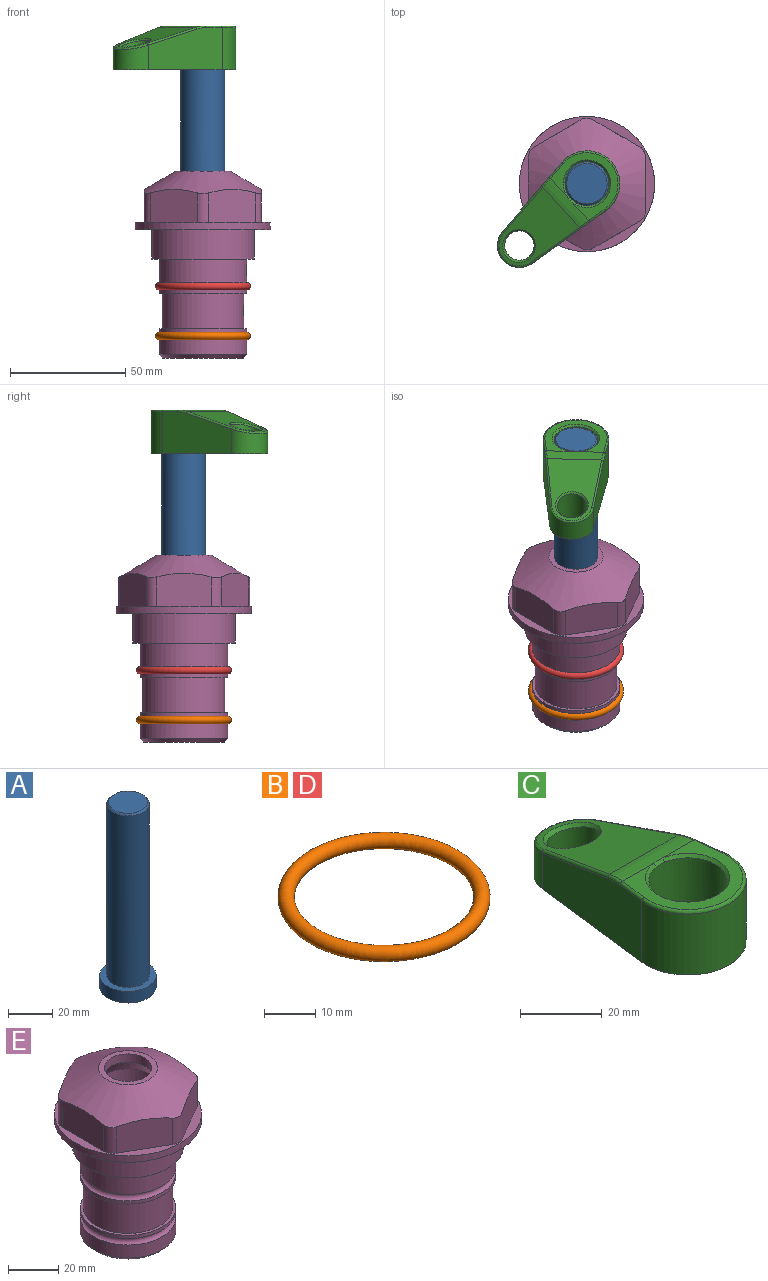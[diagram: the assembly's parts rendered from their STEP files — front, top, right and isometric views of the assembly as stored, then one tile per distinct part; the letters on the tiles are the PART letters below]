
ASSEMBLY  parts=5 mates=4
PART A: 6 faces, bbox 25.4x25.4x101.6 mm
  f0: plane 17.46x17.46mm, normal (0,0,1), area 239.5mm2, adj f5
  f1: plane 25.4x25.4mm, normal (0,0,-1), area 506.7mm2, adj f2
  f2: cylinder r=12.7mm len=25.4mm, axis (0,0,1), area 506.7mm2, adj f1,f3
  f3: plane 25.4x25.4mm, normal (0,0,1), area 221.7mm2, adj f2,f4
  f4: cylinder r=9.53mm len=94.46mm, axis (0,0,1), area 5653mm2, adj f3,f5
  f5: cone r=8.73mm half-angle=45deg, axis (0,0,-1), area 64.4mm2, adj f0,f4
PART B: 1 faces, bbox 44.7x44.7x3.2 mm
  f0: torus R=19.05mm, axis (0,0,1), area 1193.9mm2
PART C: 31 faces, bbox 31.7x65.5x19.8 mm
  f0: plane 39.12x18.26mm, normal (0.99,0.12,0), area 612.2mm2, adj f1,f4,f7,f11,f13,f15
  f1: cylinder r=9.53mm len=18.91mm, axis (0,0,-1), area 296.1mm2, adj f0,f2,f7,f17
  f2: plane 39.12x18.26mm, normal (-0.99,0.12,0), area 612.2mm2, adj f1,f4,f7,f12,f14,f16
  f3: cylinder r=6.35mm len=12.7mm, axis (0,0,-1), area 362.4mm2, adj f7,f18
  f4: cylinder r=14.29mm len=28.58mm, axis (0,0,-1), area 882.2mm2, adj f0,f2,f7,f10
  f5: cylinder r=9.53mm len=19.05mm, axis (0,0,-1), area 1092.6mm2, adj f7,f19,f20
  f6: plane 26.99x23.69mm, normal (0,0,1), area 216.2mm2, adj f9,f10,f11,f12,f19
  f7: plane 63.5x28.58mm, normal (0,0,-1), area 661.8mm2, adj f0,f1,f2,f3,f4,f5,f22,f23
  f8: plane 33.52x23.6mm, normal (0,0.26,0.97), area 486mm2, adj f9,f15,f16,f17,f18
  f9: cylinder r=19.05mm len=24.72mm, axis (1,0,0), area 120.4mm2, adj f6,f8,f13,f14,f20
  f10: torus R=13.49mm, axis (0,0,1), area 59mm2, adj f4,f6,f11,f12
  f11: cylinder r=0.79mm len=8.67mm, axis (0.12,-0.99,0), area 10.8mm2, adj f0,f6,f10,f13
  f12: cylinder r=0.79mm len=8.67mm, axis (0.12,0.99,0), area 10.8mm2, adj f2,f6,f10,f14
  f13: bspline ~4.95x1.42mm, area 6.1mm2, adj f0,f9,f11,f15
  f14: bspline ~4.95x1.42mm, area 6.1mm2, adj f2,f9,f12,f16
  f15: cylinder r=0.79mm len=25.95mm, axis (0.12,-0.96,0.26), area 32.9mm2, adj f0,f8,f13,f17
  f16: cylinder r=0.79mm len=25.95mm, axis (0.12,0.96,-0.26), area 32.9mm2, adj f2,f8,f14,f17
  f17: bspline ~18.91x8.38mm, area 30mm2, adj f1,f8,f15,f16
  f18: bspline ~14.29x14.29mm, area 48.3mm2, adj f3,f8
  f19: cone r=9.53mm half-angle=45deg, axis (0,0,1), area 66.5mm2, adj f5,f6,f20
  f20: bspline ~3.22x0.96mm, area 3.5mm2, adj f5,f9,f19
  f21: plane 2.75x2.72mm, normal (0,0,-1), area 2.9mm2, adj f23,f25,f28
  f22: plane 23.05x15.88mm, normal (-0.99,-0.12,0), area 323.6mm2, adj f7,f25,f26,f27,f28,f29
  f23: plane 23.05x15.88mm, normal (0.99,-0.12,0), area 323.6mm2, adj f7,f21,f25,f27,f28,f30
  f24: cylinder r=9.53mm len=10.69mm, axis (0,0,-1), area 114.7mm2, adj f7,f27,f29,f30
  f25: cylinder r=12.7mm len=20.59mm, axis (0,0,-1), area 381.1mm2, adj f7,f21,f22,f23,f26,f28
  f26: plane 2.75x2.72mm, normal (0,0,-1), area 2.9mm2, adj f22,f25,f28
  f27: plane 19.72x18.37mm, normal (0,-0.26,-0.97), area 291.8mm2, adj f22,f23,f24,f28,f29,f30
  f28: cylinder r=15.88mm len=19.92mm, axis (1,0,0), area 54.8mm2, adj f21,f22,f23,f25,f26,f27
  f29: cylinder r=1.59mm len=11mm, axis (0,0,-1), area 34.7mm2, adj f7,f22,f24,f27
  f30: cylinder r=1.59mm len=11mm, axis (0,0,-1), area 34.7mm2, adj f7,f23,f24,f27
PART D: same geometry as B
PART E: 36 faces, bbox 58.7x58.7x81 mm
  f0: cylinder r=17.78mm len=35.56mm, axis (0,0,1), area 1670.8mm2, adj f23,f24,f31
  f1: cylinder r=19.05mm len=38.1mm, axis (0,0,1), area 1191.9mm2, adj f26,f27,f30
  f2: plane 58.66x58.66mm, normal (0,0,-1), area 1150.6mm2, adj f3,f28
  f3: cylinder r=29.33mm len=58.66mm, axis (0,0,-1), area 585.1mm2, adj f2,f4
  f4: plane 58.66x58.66mm, normal (0,0,1), area 475.9mm2, adj f3,f5,f6,f7,f8,f9,f10,f11
  f5: plane 20.32x14.34mm, normal (-0.5,0.87,0), area 324.4mm2, adj f4,f15,f16,f17
  f6: plane 20.32x14.34mm, normal (0.5,0.87,0), area 324.4mm2, adj f4,f14,f15,f17
  f7: plane 23.48x14.34mm, normal (1,0,0), area 324.4mm2, adj f4,f13,f14,f17
  f8: plane 20.32x14.34mm, normal (0.5,-0.87,0), area 324.4mm2, adj f4,f12,f13,f17
  f9: plane 20.32x14.34mm, normal (-0.5,-0.87,0), area 324.4mm2, adj f4,f11,f12,f17
  f10: plane 23.48x14.34mm, normal (-1,0,0), area 324.4mm2, adj f4,f11,f16,f17
  f11: cylinder r=5.08mm len=12.85mm, axis (0,0,-1), area 67.2mm2, adj f4,f9,f10,f17
  f12: cylinder r=5.08mm len=12.85mm, axis (0,0,-1), area 67.2mm2, adj f4,f8,f9,f17
  f13: cylinder r=5.08mm len=12.85mm, axis (0,0,-1), area 67.2mm2, adj f4,f7,f8,f17
  f14: cylinder r=5.08mm len=12.85mm, axis (0,0,-1), area 67.2mm2, adj f4,f6,f7,f17
  f15: cylinder r=5.08mm len=12.85mm, axis (0,0,-1), area 67.2mm2, adj f4,f5,f6,f17
  f16: cylinder r=5.08mm len=12.85mm, axis (0,0,-1), area 67.2mm2, adj f4,f5,f10,f17
  f17: cone r=11.73mm half-angle=60deg, axis (0,0,-1), area 2071.8mm2, adj f5,f6,f7,f8,f9,f10,f11,f12
  f18: plane 23.46x23.46mm, normal (0,0,1), area 147.4mm2, adj f17,f35
  f19: plane 34.93x34.93mm, normal (0,0,-1), area 958mm2, adj f29
  f20: cylinder r=19.05mm len=38.1mm, axis (0,0,1), area 760.1mm2, adj f21,f29
  f21: torus R=19.05mm, axis (0,0,1), area 565.3mm2, adj f20,f22
  f22: cylinder r=19.05mm len=38.1mm, axis (0,0,1), area 190mm2, adj f21,f23
  f23: plane 38.1x38.1mm, normal (0,0,1), area 146.9mm2, adj f0,f22
  f24: plane 38.1x38.1mm, normal (0,0,-1), area 146.9mm2, adj f0,f25
  f25: cylinder r=19.05mm len=38.1mm, axis (0,0,1), area 190mm2, adj f24,f26
  f26: torus R=19.05mm, axis (0,0,1), area 565.3mm2, adj f1,f25
  f27: plane 44.45x44.45mm, normal (0,0,-1), area 411.7mm2, adj f1,f28
  f28: cylinder r=22.23mm len=44.45mm, axis (0,0,1), area 1773.5mm2, adj f2,f27
  f29: cone r=19.05mm half-angle=45deg, axis (0,0,1), area 257.5mm2, adj f19,f20
  f30: cylinder r=3.17mm len=6.75mm, axis (-1,0,0), area 128mm2, adj f1,f33
  f31: cylinder r=3.17mm len=6.35mm, axis (-1,0,0), area 102.5mm2, adj f0,f33
  f32: plane 25.4x25.4mm, normal (0,0,1), area 506.7mm2, adj f33
  f33: cylinder r=12.7mm len=66.42mm, axis (0,0,-1), area 5236.2mm2, adj f30,f31,f32,f34
  f34: cone r=9.53mm half-angle=30deg, axis (0,0,-1), area 443.4mm2, adj f33,f35
  f35: cylinder r=9.53mm len=19.05mm, axis (0,0,-1), area 240.9mm2, adj f18,f34
PLACE A rot(axis=(0,0,1),132.5deg) t=(0,0,24.06)mm
PLACE B t=(0,0,-21.59)mm
PLACE C rot(axis=(0,0,1),132.5deg) t=(0,0,24.86)mm
PLACE D at identity
PLACE E at identity fixed
MATE cylindrical A.f2 <-> E.f0  axis (0,0,-1) through (0,0,-14.04)mm
MATE fastened C.f4 <-> A.f2  axis (0,0,-1) through (0,0,87.56)mm
MATE fastened B.f0 <-> E.f0  axis (0,0,1) through (0,0,-46.1)mm
MATE fastened D.f0 <-> E.f0  axis (0,0,1) through (0,0,-24.51)mm
